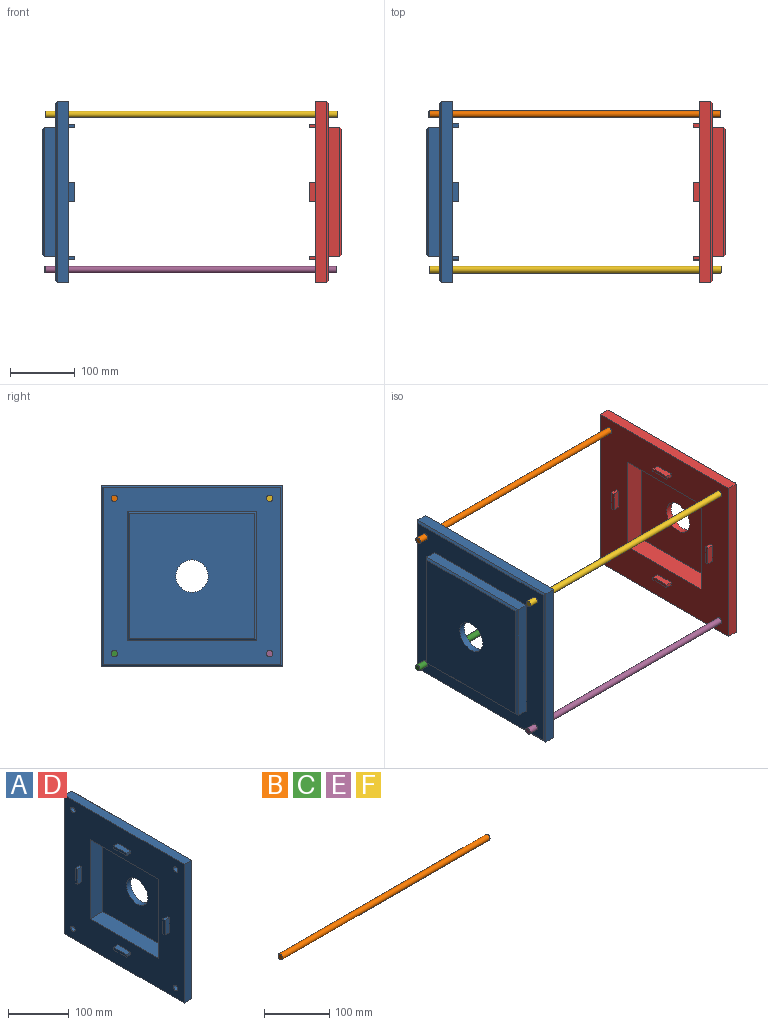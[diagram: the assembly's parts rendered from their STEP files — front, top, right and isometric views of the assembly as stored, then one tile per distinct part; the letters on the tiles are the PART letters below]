
ASSEMBLY  parts=6 mates=6
PART A: 49 faces, bbox 50x280x280 mm
  f0: plane 280x280mm, normal (-1,0,0), area 51885.8mm2, adj f1,f2,f3,f4,f5,f6,f7,f8
  f1: plane 280x17mm, normal (0,0,1), area 4760mm2, adj f0,f2,f8,f45
  f2: plane 280x17mm, normal (0,-1,0), area 4760mm2, adj f0,f1,f3,f46
  f3: plane 280x17mm, normal (0,0,-1), area 4760mm2, adj f0,f2,f8,f48
  f4: cylinder r=5mm len=20mm, axis (-1,0,0), area 628.3mm2, adj f0,f9
  f5: cylinder r=5mm len=20mm, axis (-1,0,0), area 628.3mm2, adj f0,f9
  f6: cylinder r=5mm len=20mm, axis (-1,0,0), area 628.3mm2, adj f0,f9
  f7: cylinder r=5mm len=20mm, axis (-1,0,0), area 628.3mm2, adj f0,f9
  f8: plane 280x17mm, normal (0,1,0), area 4760mm2, adj f0,f1,f3,f47
  f9: plane 274x274mm, normal (1,0,0), area 34761.8mm2, adj f4,f5,f6,f7,f10,f11,f12,f13
  f10: plane 200x17mm, normal (0,0,1), area 3400mm2, adj f9,f11,f13,f42
  f11: plane 200x17mm, normal (0,-1,0), area 3400mm2, adj f9,f10,f12,f41
  f12: plane 200x17mm, normal (0,0,-1), area 3400mm2, adj f9,f11,f13,f43
  f13: plane 200x17mm, normal (0,1,0), area 3400mm2, adj f9,f10,f12,f44
  f14: cylinder r=25mm len=50mm, axis (-1,0,0), area 1570.8mm2, adj f15,f20
  f15: plane 194x194mm, normal (1,0,0), area 35672.5mm2, adj f14,f41,f42,f43,f44
  f16: plane 160x30mm, normal (0,0,-1), area 4800mm2, adj f0,f17,f19,f20
  f17: plane 160x30mm, normal (0,1,0), area 4800mm2, adj f0,f16,f18,f20
  f18: plane 160x30mm, normal (0,0,1), area 4800mm2, adj f0,f17,f19,f20
  f19: plane 160x30mm, normal (0,-1,0), area 4800mm2, adj f0,f16,f18,f20
  f20: plane 160x160mm, normal (-1,0,0), area 23636.5mm2, adj f14,f16,f17,f18,f19
  f21: plane 10x5mm, normal (0,-1,0), area 50mm2, adj f0,f22,f24,f25
  f22: plane 30x10mm, normal (0,0,-1), area 300mm2, adj f0,f21,f23,f25
  f23: plane 10x5mm, normal (0,1,0), area 50mm2, adj f0,f22,f24,f25
  f24: plane 30x10mm, normal (0,0,1), area 300mm2, adj f0,f21,f23,f25
  f25: plane 30x5mm, normal (-1,0,0), area 150mm2, adj f21,f22,f23,f24
  f26: plane 30x10mm, normal (0,0,-1), area 300mm2, adj f0,f27,f29,f30
  f27: plane 10x5mm, normal (0,1,0), area 50mm2, adj f0,f26,f28,f30
  f28: plane 30x10mm, normal (0,0,1), area 300mm2, adj f0,f27,f29,f30
  f29: plane 10x5mm, normal (0,-1,0), area 50mm2, adj f0,f26,f28,f30
  f30: plane 30x5mm, normal (-1,0,0), area 150mm2, adj f26,f27,f28,f29
  f31: plane 10x5mm, normal (0,0,1), area 50mm2, adj f0,f32,f34,f35
  f32: plane 30x10mm, normal (0,-1,0), area 300mm2, adj f0,f31,f33,f35
  f33: plane 10x5mm, normal (0,0,-1), area 50mm2, adj f0,f32,f34,f35
  f34: plane 30x10mm, normal (0,1,0), area 300mm2, adj f0,f31,f33,f35
  f35: plane 30x5mm, normal (-1,0,0), area 150mm2, adj f31,f32,f33,f34
  f36: plane 30x10mm, normal (0,1,0), area 300mm2, adj f0,f37,f39,f40
  f37: plane 10x5mm, normal (0,0,1), area 50mm2, adj f0,f36,f38,f40
  f38: plane 30x10mm, normal (0,-1,0), area 300mm2, adj f0,f37,f39,f40
  f39: plane 10x5mm, normal (0,0,-1), area 50mm2, adj f0,f36,f38,f40
  f40: plane 30x5mm, normal (-1,0,0), area 150mm2, adj f36,f37,f38,f39
  f41: plane 200x3mm, normal (0.71,-0.71,0), area 835.8mm2, adj f11,f15,f42,f43
  f42: plane 200x3mm, normal (0.71,0,0.71), area 835.8mm2, adj f10,f15,f41,f44
  f43: plane 200x3mm, normal (0.71,0,-0.71), area 835.8mm2, adj f12,f15,f41,f44
  f44: plane 200x3mm, normal (0.71,0.71,0), area 835.8mm2, adj f13,f15,f42,f43
  f45: plane 280x3mm, normal (0.71,0,0.71), area 1175.2mm2, adj f1,f9,f46,f47
  f46: plane 280x3mm, normal (0.71,-0.71,0), area 1175.2mm2, adj f2,f9,f45,f48
  f47: plane 280x3mm, normal (0.71,0.71,0), area 1175.2mm2, adj f8,f9,f45,f48
  f48: plane 280x3mm, normal (0.71,0,-0.71), area 1175.2mm2, adj f3,f9,f46,f47
PART B: 3 faces, bbox 450x10x10 mm
  f0: cylinder r=5mm len=450mm, axis (-1,0,0), area 14137.2mm2, adj f1,f2
  f1: plane 10x10mm, normal (1,0,0), area 78.5mm2, adj f0
  f2: plane 10x10mm, normal (-1,0,0), area 78.5mm2, adj f0
PART C: same geometry as B
PART D: same geometry as A
PART E: same geometry as B
PART F: same geometry as B
PLACE A rot(axis=(0,0,1),180deg) t=(512.77,376.86,-22.29)mm
PLACE B t=(476.77,496.86,97.71)mm
PLACE C t=(475.66,496.86,-142.29)mm
PLACE D t=(894.66,376.86,-22.29)mm
PLACE E t=(476.77,256.86,-142.29)mm
PLACE F t=(477.66,256.86,97.71)mm
MATE slider A.f4 <-> F.f0  axis (1,0,0) through (512.77,256.86,97.71)mm
MATE slider C.f0 <-> A.f6  axis (-1,0,0) through (475.66,496.86,-142.29)mm
MATE slider F.f0 <-> D.f7  axis (1,0,0) through (927.66,256.86,97.71)mm
MATE slider B.f0 <-> A.f7  axis (-1,0,0) through (476.77,496.86,97.71)mm
MATE slider E.f0 <-> A.f5  axis (-1,0,0) through (476.77,256.86,-142.29)mm
MATE slider C.f0 <-> D.f5  axis (1,0,0) through (925.66,496.86,-142.29)mm
